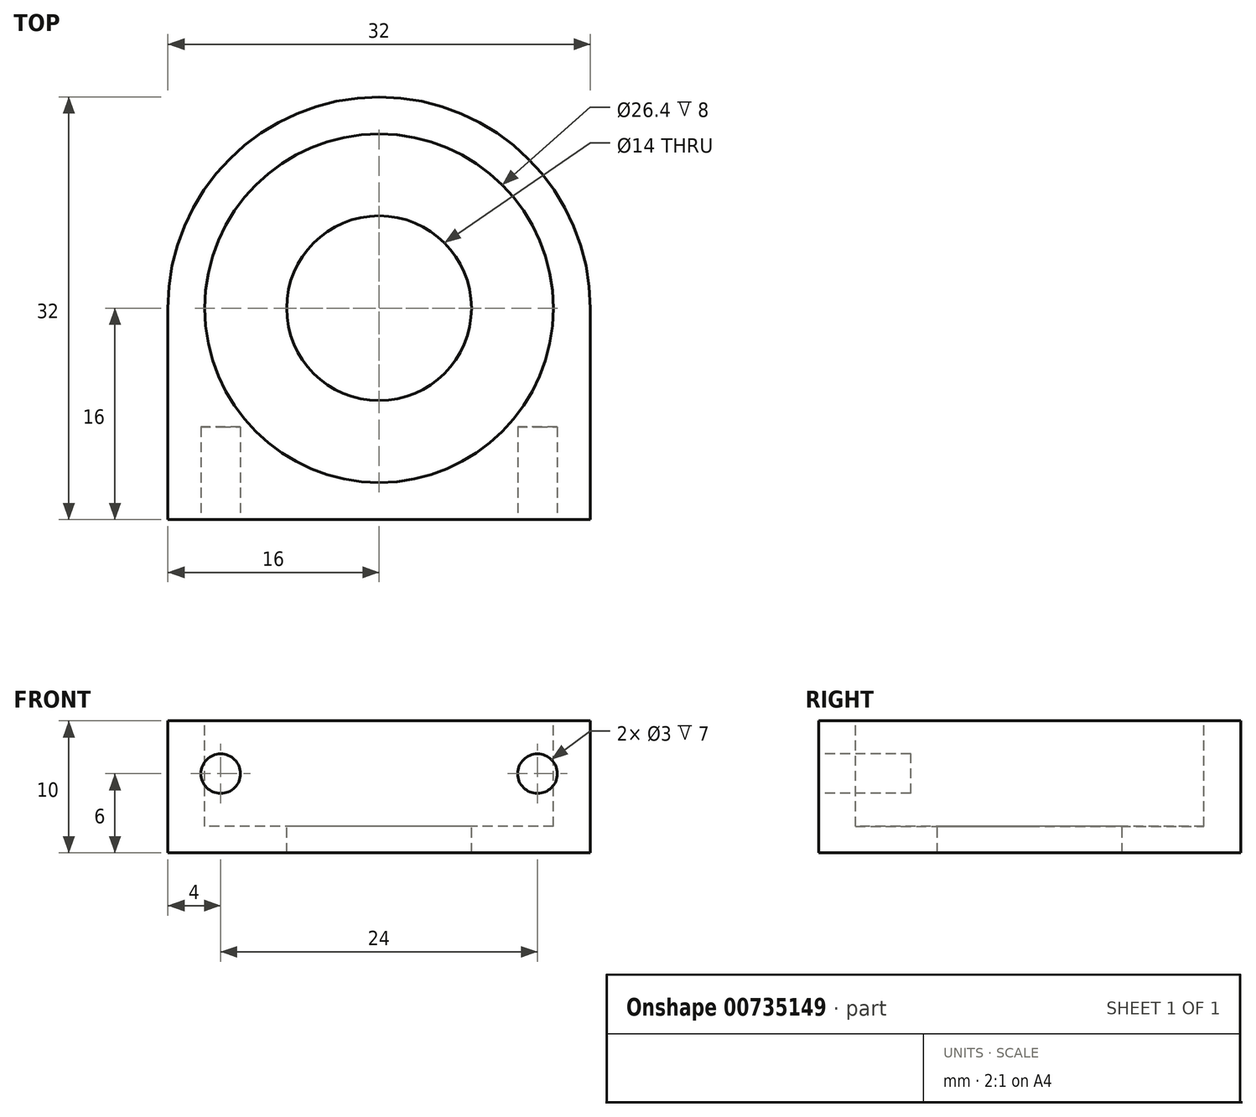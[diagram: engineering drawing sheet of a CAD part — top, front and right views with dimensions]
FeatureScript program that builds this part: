
annotation { "Feature Type Name" : "Feature", "Feature Type Description" : "" }
export const myFeature = defineFeature(function(context is Context, id is Id, definition is map)
    precondition{}
    {
        {
            var Q0;
            Q0=qCreatedBy(makeId("Top.planeOp"),FACE);
            var sketch = newSketch(context, id + "F0", { "sketchPlane" : qUnion([Q0])});
            skCircle(sketch, "E0", {"center": v(0, 0) * mm, "radius": 16 * mm});
            skSolve(sketch);
        }
        {
            var Q0;
            Q0=makeQuery(id+"F0.imprint","IMPRINT",FACE,{"disambiguationData":[TD([[makeQuery(id+"F0.imprint","IMPRINT",EDGE,{"derivedFrom":sQuery(id+"F0.wireOp",EDGE,"E0")}),1.0]])]});
            extrude(context, id + "F1", {"entities" : qUnion([Q0]), "depth" : 10 * mm, "offsetDistance" : 25 * mm});
        }
        {
            var Q0;
            Q0=makeQuery(id+"F1.opExtrude","CAP_FACE",FACE,{"disambiguationData":[OSD([sQuery(id+"F0.wireOp",EDGE,"E0")])],"isStart":false});
            var sketch = newSketch(context, id + "F2", { "sketchPlane" : qUnion([Q0])});
            skLineSegment(sketch, "E1.bottom", {"start": v(-16, 0) * mm, "end": v(16, 0) * mm});
            skLineSegment(sketch, "E1.top", {"start": v(-16, -16) * mm, "end": v(16, -16) * mm});
            skLineSegment(sketch, "E1.left", {"start": v(-16, 0) * mm, "end": v(-16, -16) * mm});
            skLineSegment(sketch, "E1.right", {"start": v(16, 0) * mm, "end": v(16, -16) * mm});
            skSolve(sketch);
        }
        {
            var Q0;
            Q0 = qSketchRegion(id + "F2", true);
            extrude(context, id + "F3", {"entities" : qUnion([Q0]), "operationType" : NewBodyOperationType.ADD, "oppositeDirection" : true, "depth" : 10 * mm, "offsetDistance" : 25 * mm});
        }
        {
            var Q0;
            Q0=makeQuery(id+"F3.boolean.opBoolean","MERGE",FACE,{"derivedFrom":[makeQuery(id+"F1.opExtrude","CAP_FACE",FACE,{"disambiguationData":[OSD([sQuery(id+"F0.wireOp",EDGE,"E0")])],"isStart":false}),makeQuery(id+"F3.opExtrude","CAP_FACE",FACE,{"disambiguationData":[OSD([sQuery(id+"F2.wireOp",EDGE,"E1.bottom"),sQuery(id+"F2.wireOp",EDGE,"E1.top"),sQuery(id+"F2.wireOp",EDGE,"E1.left"),sQuery(id+"F2.wireOp",EDGE,"E1.right")])],"isStart":true})]});
            var sketch = newSketch(context, id + "F4", { "sketchPlane" : qUnion([Q0])});
            skCircle(sketch, "E2", {"center": v(0, 0) * mm, "radius": 13.2 * mm});
            skSolve(sketch);
        }
        {
            var Q0;
            Q0=makeQuery(id+"F4.imprint","IMPRINT",FACE,{"disambiguationData":[TD([[makeQuery(id+"F4.imprint","IMPRINT",EDGE,{"derivedFrom":sQuery(id+"F4.wireOp",EDGE,"E2")}),1.0]])]});
            extrude(context, id + "F5", {"entities" : qUnion([Q0]), "operationType" : NewBodyOperationType.REMOVE, "oppositeDirection" : true, "depth" : 8 * mm, "offsetDistance" : 25 * mm});
        }
        {
            var Q0;
            Q0=makeQuery(id+"F5.boolean.opBoolean","COPY",FACE,{"derivedFrom":makeQuery(id+"F5.opExtrude","CAP_FACE",FACE,{"disambiguationData":[OSD([sQuery(id+"F4.wireOp",EDGE,"E2")])],"isStart":false})});
            var sketch = newSketch(context, id + "F6", { "sketchPlane" : qUnion([Q0])});
            skCircle(sketch, "E3", {"center": v(0, 0) * mm, "radius": 7 * mm});
            skSolve(sketch);
        }
        {
            var Q0;
            Q0=makeQuery(id+"F6.imprint","IMPRINT",FACE,{"disambiguationData":[TD([[makeQuery(id+"F6.imprint","IMPRINT",EDGE,{"derivedFrom":sQuery(id+"F6.wireOp",EDGE,"E3")}),1.0]])]});
            extrude(context, id + "F7", {"entities" : qUnion([Q0]), "operationType" : NewBodyOperationType.REMOVE, "oppositeDirection" : true, "depth" : 25 * mm, "offsetDistance" : 25 * mm});
        }
        {
            var Q0;
            Q0=makeQuery(id+"F3.opExtrude","SWEPT_FACE",FACE,{"disambiguationData":[OSD([sQuery(id+"F2.wireOp",EDGE,"E1.top")])]});
            var sketch = newSketch(context, id + "F8", { "sketchPlane" : qUnion([Q0])});
            skCircle(sketch, "E4", {"center": v(-12, 6) * mm, "radius": 1.5 * mm});
            skCircle(sketch, "E5", {"center": v(12, 6) * mm, "radius": 1.5 * mm});
            skSolve(sketch);
        }
        {
            var Q0;
            Q0=makeQuery(id+"F8.imprint","IMPRINT",FACE,{"disambiguationData":[TD([[makeQuery(id+"F8.imprint","IMPRINT",EDGE,{"derivedFrom":sQuery(id+"F8.wireOp",EDGE,"E4")}),1.0]])]});
            var Q1;
            Q1=makeQuery(id+"F8.imprint","IMPRINT",FACE,{"disambiguationData":[TD([[makeQuery(id+"F8.imprint","IMPRINT",EDGE,{"derivedFrom":sQuery(id+"F8.wireOp",EDGE,"E5")}),1.0]])]});
            extrude(context, id + "F9", {"entities" : qUnion([Q0, Q1]), "operationType" : NewBodyOperationType.REMOVE, "oppositeDirection" : true, "depth" : 7 * mm, "offsetDistance" : 25 * mm});
        }
    });
